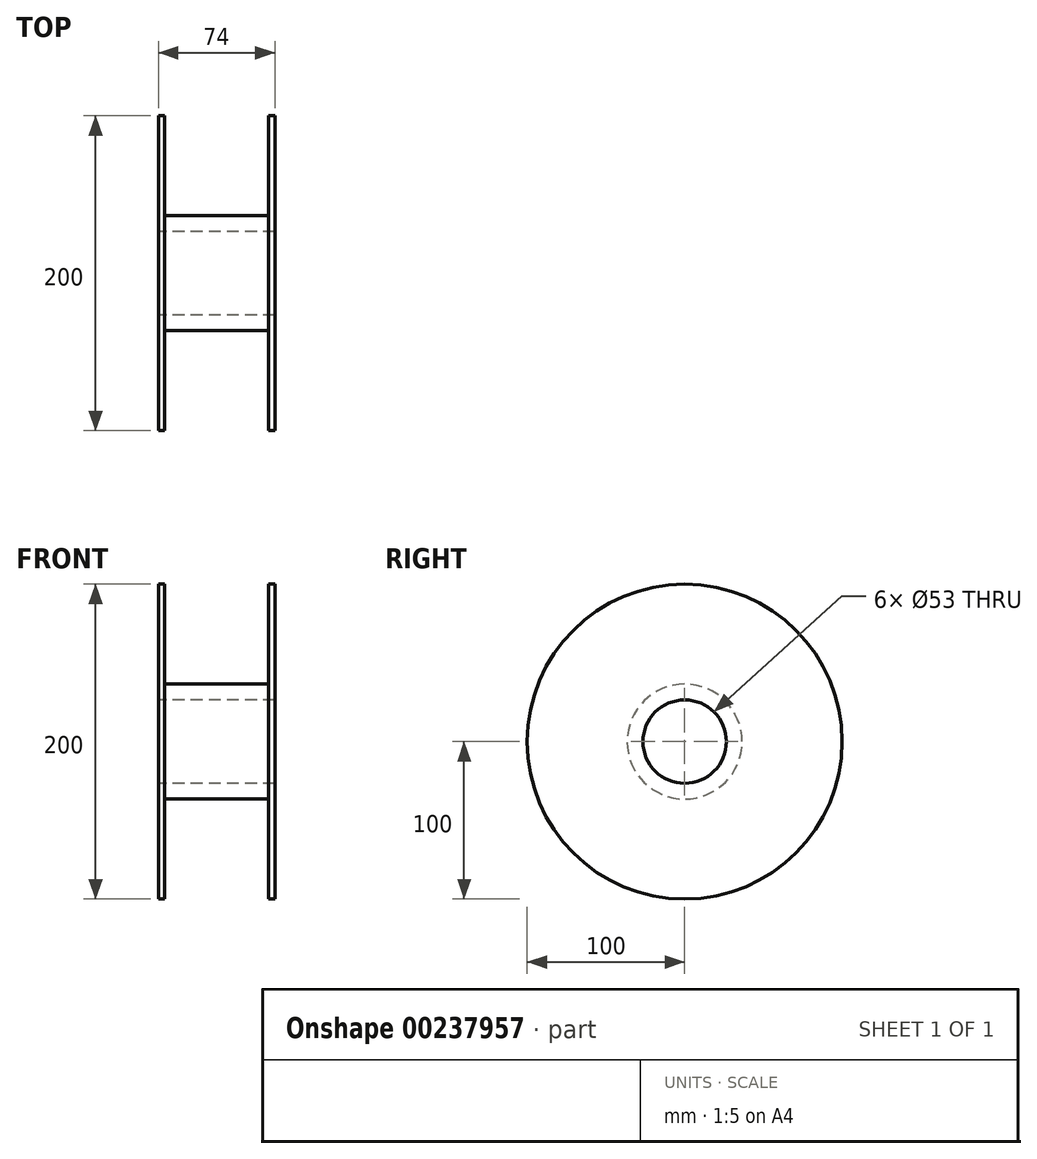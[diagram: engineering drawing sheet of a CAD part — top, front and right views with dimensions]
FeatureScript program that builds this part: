
annotation { "Feature Type Name" : "Feature", "Feature Type Description" : "" }
export const myFeature = defineFeature(function(context is Context, id is Id, definition is map)
    precondition{}
    {
        {
            var Q0;
            Q0=qCreatedBy(makeId("Right.planeOp"),FACE);
            var sketch = newSketch(context, id + "F0", { "sketchPlane" : qUnion([Q0])});
            skCircle(sketch, "E0", {"center": v(0, 0) * mm, "radius": 100 * mm});
            skCircle(sketch, "E1", {"center": v(0, 0) * mm, "radius": 26.5 * mm});
            skSolve(sketch);
        }
        {
            var Q0;
            Q0 = qSketchRegion(id + "F0", true);
            extrude(context, id + "F1", {"entities" : qUnion([Q0]), "depth" : 74 * mm});
        }
        {
            var Q0;
            Q0=qCreatedBy(makeId("Right.planeOp"),FACE);
            cPlane(context, id + "F2", {"entities" : qUnion([Q0]), "cplaneType" : CPlaneType.OFFSET, "offset" : 37 * mm, "width" : 150 * mm, "height" : 150 * mm});
        }
        {
            var Q0;
            Q0=qCreatedBy(id+"F2.planeOp",FACE);
            var sketch = newSketch(context, id + "F3", { "sketchPlane" : qUnion([Q0])});
            skCircle(sketch, "E2.0", {"center": v(0, 0) * mm, "radius": 100 * mm});
            skCircle(sketch, "E3.0", {"center": v(0, 0) * mm, "radius": 26.5 * mm, "construction": true});
            skCircle(sketch, "E4.0", {"center": v(0, 0) * mm, "radius": 36.5 * mm});
            skSolve(sketch);
        }
        {
            var Q0;
            Q0 = qSketchRegion(id + "F3", true);
            extrude(context, id + "F4", {"entities" : qUnion([Q0]), "operationType" : NewBodyOperationType.REMOVE, "oppositeDirection" : true, "depth" : 33 * mm, "hasSecondDirection" : true, "secondDirectionOppositeDirection" : false, "secondDirectionDepth" : 33 * mm});
        }
    });
